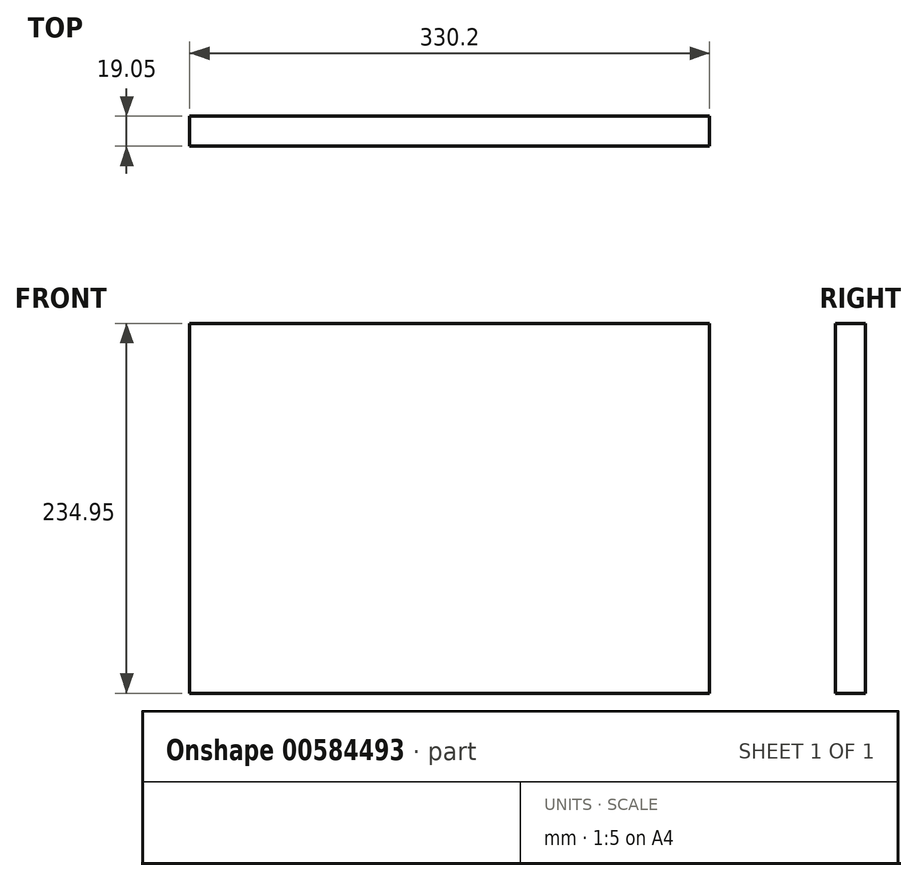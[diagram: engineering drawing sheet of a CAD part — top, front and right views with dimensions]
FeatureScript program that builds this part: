
annotation { "Feature Type Name" : "Feature", "Feature Type Description" : "" }
export const myFeature = defineFeature(function(context is Context, id is Id, definition is map)
    precondition{}
    {
        {
            var Q0;
            Q0=qCreatedBy(makeId("Front.planeOp"),FACE);
            var sketch = newSketch(context, id + "F0", { "sketchPlane" : qUnion([Q0])});
            skLineSegment(sketch, "E0.bottom", {"start": v(0, 0) * mm, "end": v(330.2, 0) * mm});
            skLineSegment(sketch, "E0.top", {"start": v(0, 234.95) * mm, "end": v(330.2, 234.95) * mm});
            skLineSegment(sketch, "E0.left", {"start": v(0, 0) * mm, "end": v(0, 234.95) * mm});
            skLineSegment(sketch, "E0.right", {"start": v(330.2, 0) * mm, "end": v(330.2, 234.95) * mm});
            skSolve(sketch);
        }
        {
            var Q0;
            Q0=makeQuery(id+"F0.imprint","IMPRINT",FACE,{"disambiguationData":[TD([[makeQuery(id+"F0.imprint","IMPRINT",EDGE,{"derivedFrom":sQuery(id+"F0.wireOp",EDGE,"E0.bottom")}),1.0]])]});
            extrude(context, id + "F1", {"entities" : qUnion([Q0]), "depth" : 19.05 * mm, "offsetDistance" : 25.4 * mm});
        }
    });
